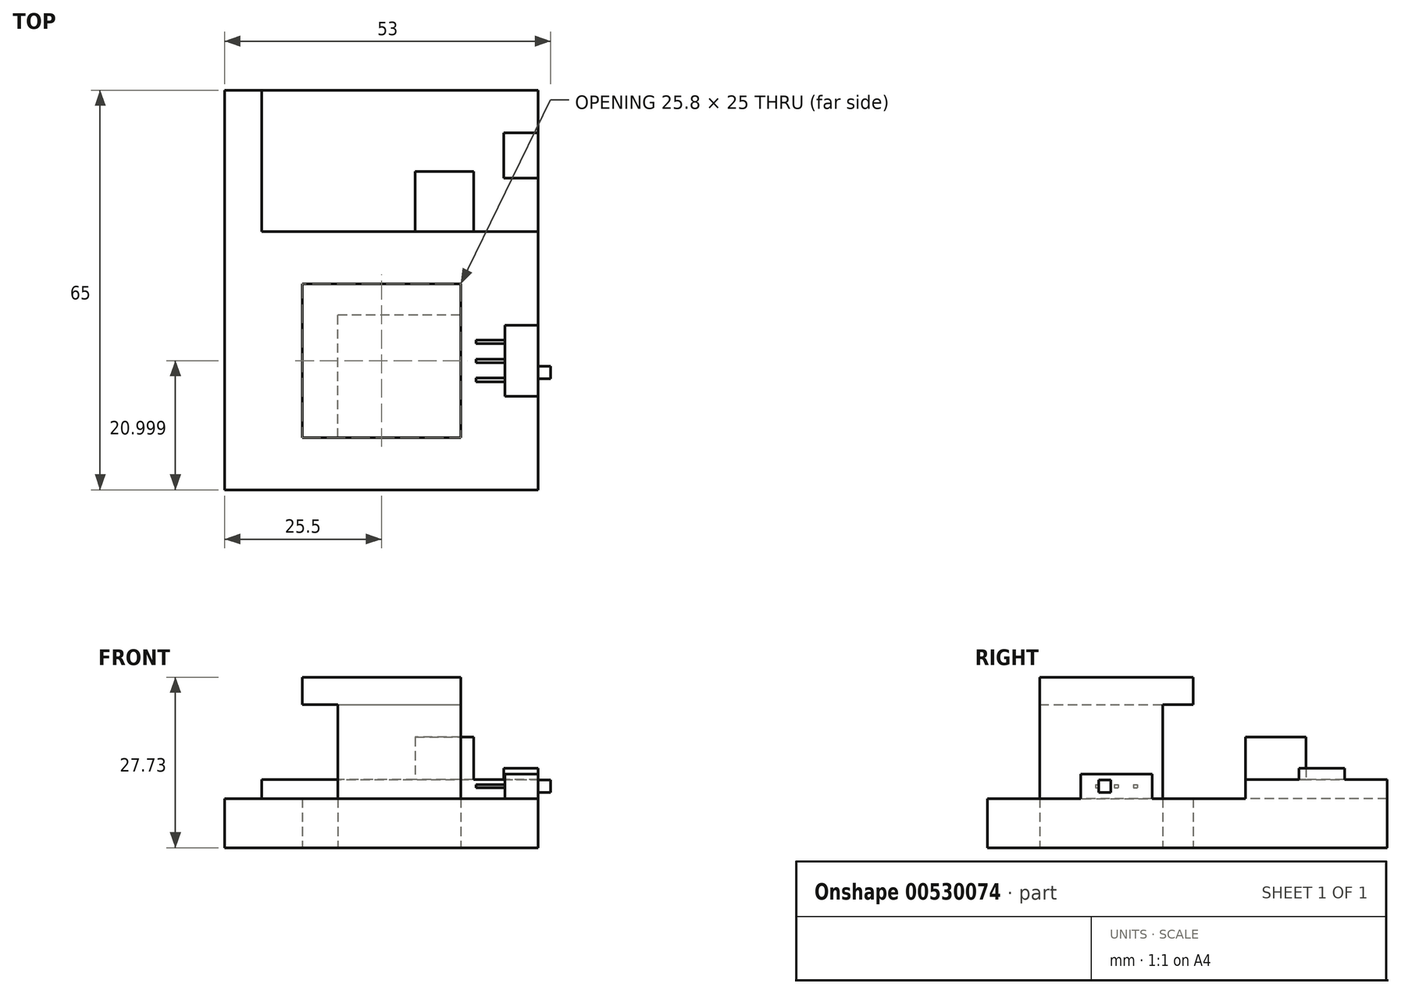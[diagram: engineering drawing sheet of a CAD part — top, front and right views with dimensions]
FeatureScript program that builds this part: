
annotation { "Feature Type Name" : "Feature", "Feature Type Description" : "" }
export const myFeature = defineFeature(function(context is Context, id is Id, definition is map)
    precondition{}
    {
        {
            var Q0;
            Q0=qCreatedBy(makeId("Top.planeOp"),FACE);
            var sketch = newSketch(context, id + "F0", { "sketchPlane" : qUnion([Q0])});
            skLineSegment(sketch, "E0", {"start": v(-31, 10.76) * mm, "end": v(20, 10.76) * mm});
            skLineSegment(sketch, "E1", {"start": v(20, 10.76) * mm, "end": v(20, -54.24) * mm});
            skLineSegment(sketch, "E2", {"start": v(-31, -54.24) * mm, "end": v(-31, 10.76) * mm});
            skLineSegment(sketch, "E3", {"start": v(-31, -54.24) * mm, "end": v(20, -54.24) * mm});
            skLineSegment(sketch, "E4", {"start": v(20, -12.24) * mm, "end": v(-25, -12.24) * mm});
            skLineSegment(sketch, "E5", {"start": v(-25, -12.24) * mm, "end": v(-25, 10.76) * mm});
            skLineSegment(sketch, "E6", {"start": v(20, -3.55) * mm, "end": v(14.37, -3.55) * mm});
            skLineSegment(sketch, "E7", {"start": v(14.37, -3.55) * mm, "end": v(14.37, 3.85) * mm});
            skLineSegment(sketch, "E8", {"start": v(14.37, 3.85) * mm, "end": v(20, 3.85) * mm});
            skLineSegment(sketch, "E9", {"start": v(0, -12.24) * mm, "end": v(0, -2.44) * mm});
            skLineSegment(sketch, "E10", {"start": v(0, -2.44) * mm, "end": v(9.5, -2.44) * mm});
            skLineSegment(sketch, "E11", {"start": v(9.5, -2.44) * mm, "end": v(9.5, -12.24) * mm});
            skLineSegment(sketch, "E12", {"start": v(-18.4, -45.74) * mm, "end": v(7.4, -45.74) * mm});
            skLineSegment(sketch, "E13", {"start": v(-18.4, -20.74) * mm, "end": v(7.4, -20.74) * mm});
            skLineSegment(sketch, "E14", {"start": v(7.4, -45.74) * mm, "end": v(7.4, -20.74) * mm});
            skLineSegment(sketch, "E15", {"start": v(-18.4, -45.74) * mm, "end": v(-18.4, -20.74) * mm});
            skLineSegment(sketch, "E16", {"start": v(-12.6, -45.74) * mm, "end": v(-12.6, -25.74) * mm});
            skLineSegment(sketch, "E17", {"start": v(-12.6, -25.74) * mm, "end": v(7.4, -25.74) * mm});
            skLineSegment(sketch, "E18", {"start": v(14.6, -39.04) * mm, "end": v(20, -39.04) * mm});
            skLineSegment(sketch, "E19", {"start": v(14.6, -27.44) * mm, "end": v(20, -27.44) * mm});
            skLineSegment(sketch, "E20", {"start": v(14.6, -39.04) * mm, "end": v(14.6, -27.44) * mm});
            skPoint(sketch, "E21.orphan", {"position": v(7.4, -39.04) * mm});
            skPoint(sketch, "E22.orphan", {"position": v(7.4, -27.44) * mm});
            skLineSegment(sketch, "E23", {"start": v(9.9, -33.57) * mm, "end": v(14.6, -33.57) * mm});
            skLineSegment(sketch, "E24", {"start": v(9.9, -32.97) * mm, "end": v(14.6, -32.97) * mm});
            skLineSegment(sketch, "E25", {"start": v(9.9, -33.57) * mm, "end": v(9.9, -32.97) * mm});
            skLineSegment(sketch, "E26", {"start": v(14.6, -30.46) * mm, "end": v(9.9, -30.47) * mm});
            skLineSegment(sketch, "E27", {"start": v(9.9, -30.47) * mm, "end": v(9.9, -29.87) * mm});
            skLineSegment(sketch, "E28", {"start": v(9.9, -29.87) * mm, "end": v(14.6, -29.86) * mm});
            skLineSegment(sketch, "E29", {"start": v(14.6, -36.07) * mm, "end": v(9.9, -36.07) * mm});
            skLineSegment(sketch, "E30", {"start": v(9.9, -36.07) * mm, "end": v(9.9, -36.67) * mm});
            skLineSegment(sketch, "E31", {"start": v(9.9, -36.67) * mm, "end": v(14.6, -36.67) * mm});
            skLineSegment(sketch, "E32", {"start": v(20, -36.14) * mm, "end": v(22, -36.14) * mm});
            skLineSegment(sketch, "E33", {"start": v(22, -36.14) * mm, "end": v(22, -34.14) * mm});
            skLineSegment(sketch, "E34", {"start": v(22, -34.14) * mm, "end": v(20, -34.14) * mm});
            skSolve(sketch);
        }
        {
            var Q0;
            {var subQ10=sQuery(id+"F0.wireOp",EDGE,"E2");Q0=makeQuery(id+"F0.imprint","IMPRINT",FACE,{"disambiguationData":[TD([[makeQuery(id+"F0.imprint","IMPRINT",EDGE,{"derivedFrom":subQ10}),-1.0]])]});}
            var Q1;
            {var subQ3=sQuery(id+"F0.wireOp",EDGE,"E16");Q1=makeQuery(id+"F0.imprint","IMPRINT",FACE,{"disambiguationData":[TD([[makeQuery(id+"F0.imprint","IMPRINT",EDGE,{"derivedFrom":subQ3}),-1.0]])]});}
            var Q2;
            {var subQ1=sQuery(id+"F0.wireOp",EDGE,"E13");Q2=makeQuery(id+"F0.imprint","IMPRINT",FACE,{"disambiguationData":[TD([[makeQuery(id+"F0.imprint","IMPRINT",EDGE,{"derivedFrom":subQ1}),-1.0]])]});}
            var Q3;
            {var subQ1=sQuery(id+"F0.wireOp",EDGE,"E5");Q3=makeQuery(id+"F0.imprint","IMPRINT",FACE,{"disambiguationData":[TD([[makeQuery(id+"F0.imprint","IMPRINT",EDGE,{"derivedFrom":subQ1}),-1.0]])]});}
            var Q4;
            {var subQ0=sQuery(id+"F0.wireOp",EDGE,"E9");Q4=makeQuery(id+"F0.imprint","IMPRINT",FACE,{"disambiguationData":[TD([[makeQuery(id+"F0.imprint","IMPRINT",EDGE,{"derivedFrom":subQ0}),-1.0]])]});}
            var Q5;
            {var subQ0=sQuery(id+"F0.wireOp",EDGE,"E6");Q5=makeQuery(id+"F0.imprint","IMPRINT",FACE,{"disambiguationData":[TD([[makeQuery(id+"F0.imprint","IMPRINT",EDGE,{"derivedFrom":subQ0}),-1.0]])]});}
            var Q6;
            {var subQ6=sQuery(id+"F0.wireOp",EDGE,"E18");Q6=makeQuery(id+"F0.imprint","IMPRINT",FACE,{"disambiguationData":[TD([[makeQuery(id+"F0.imprint","IMPRINT",EDGE,{"derivedFrom":subQ6}),1.0]])]});}
            var Q7;
            {var subQ0=sQuery(id+"F0.wireOp",EDGE,"E29");Q7=makeQuery(id+"F0.imprint","IMPRINT",FACE,{"disambiguationData":[TD([[makeQuery(id+"F0.imprint","IMPRINT",EDGE,{"derivedFrom":subQ0}),1.0]])]});}
            var Q8;
            {var subQ0=sQuery(id+"F0.wireOp",EDGE,"E23");Q8=makeQuery(id+"F0.imprint","IMPRINT",FACE,{"disambiguationData":[TD([[makeQuery(id+"F0.imprint","IMPRINT",EDGE,{"derivedFrom":subQ0}),1.0]])]});}
            var Q9;
            {var subQ0=sQuery(id+"F0.wireOp",EDGE,"E26");Q9=makeQuery(id+"F0.imprint","IMPRINT",FACE,{"disambiguationData":[TD([[makeQuery(id+"F0.imprint","IMPRINT",EDGE,{"derivedFrom":subQ0}),-1.0]])]});}
            extrude(context, id + "F1", {"entities" : qUnion([Q0, Q1, Q2, Q3, Q4, Q5, Q6, Q7, Q8, Q9]), "depth" : 8 * mm, "offsetDistance" : 25 * mm});
        }
        {
            var Q0;
            {var subQ2=sQuery(id+"F0.wireOp",EDGE,"E5");Q0=makeQuery(id+"F0.imprint","IMPRINT",FACE,{"disambiguationData":[TD([[makeQuery(id+"F0.imprint","IMPRINT",EDGE,{"derivedFrom":subQ2}),-1.0]])]});}
            var Q1;
            {var subQ0=sQuery(id+"F0.wireOp",EDGE,"E9");Q1=makeQuery(id+"F0.imprint","IMPRINT",FACE,{"disambiguationData":[TD([[makeQuery(id+"F0.imprint","IMPRINT",EDGE,{"derivedFrom":subQ0}),-1.0]])]});}
            var Q2;
            {var subQ0=sQuery(id+"F0.wireOp",EDGE,"E6");Q2=makeQuery(id+"F0.imprint","IMPRINT",FACE,{"disambiguationData":[TD([[makeQuery(id+"F0.imprint","IMPRINT",EDGE,{"derivedFrom":subQ0}),-1.0]])]});}
            extrude(context, id + "F2", {"entities" : qUnion([Q0, Q1, Q2]), "operationType" : NewBodyOperationType.ADD, "depth" : 11.1 * mm, "offsetDistance" : 25 * mm});
        }
        {
            var Q0;
            {var subQ0=sQuery(id+"F0.wireOp",EDGE,"E6");Q0=makeQuery(id+"F0.imprint","IMPRINT",FACE,{"disambiguationData":[TD([[makeQuery(id+"F0.imprint","IMPRINT",EDGE,{"derivedFrom":subQ0}),-1.0]])]});}
            extrude(context, id + "F3", {"entities" : qUnion([Q0]), "operationType" : NewBodyOperationType.ADD, "depth" : 12.95 * mm, "offsetDistance" : 25 * mm});
        }
        {
            var Q0;
            {var subQ0=sQuery(id+"F0.wireOp",EDGE,"E9");Q0=makeQuery(id+"F0.imprint","IMPRINT",FACE,{"disambiguationData":[TD([[makeQuery(id+"F0.imprint","IMPRINT",EDGE,{"derivedFrom":subQ0}),-1.0]])]});}
            extrude(context, id + "F4", {"entities" : qUnion([Q0]), "operationType" : NewBodyOperationType.ADD, "depth" : 18 * mm, "offsetDistance" : 25 * mm});
        }
        {
            var Q0;
            {var subQ3=sQuery(id+"F0.wireOp",EDGE,"E16");Q0=makeQuery(id+"F0.imprint","IMPRINT",FACE,{"disambiguationData":[TD([[makeQuery(id+"F0.imprint","IMPRINT",EDGE,{"derivedFrom":subQ3}),-1.0]])]});}
            extrude(context, id + "F5", {"entities" : qUnion([Q0]), "operationType" : NewBodyOperationType.ADD, "depth" : 23.3 * mm, "offsetDistance" : 25 * mm});
        }
        {
            var Q0;
            {var subQ3=sQuery(id+"F0.wireOp",EDGE,"E16");Q0=makeQuery(id+"F0.imprint","IMPRINT",FACE,{"disambiguationData":[TD([[makeQuery(id+"F0.imprint","IMPRINT",EDGE,{"derivedFrom":subQ3}),-1.0]])]});}
            var Q1;
            {var subQ1=sQuery(id+"F0.wireOp",EDGE,"E13");Q1=makeQuery(id+"F0.imprint","IMPRINT",FACE,{"disambiguationData":[TD([[makeQuery(id+"F0.imprint","IMPRINT",EDGE,{"derivedFrom":subQ1}),-1.0]])]});}
            extrude(context, id + "F6", {"entities" : qUnion([Q0, Q1]), "operationType" : NewBodyOperationType.ADD, "depth" : 27.73 * mm, "offsetDistance" : 25 * mm});
        }
        {
            var Q0;
            {var subQ1=sQuery(id+"F0.wireOp",EDGE,"E13");Q0=makeQuery(id+"F0.imprint","IMPRINT",FACE,{"disambiguationData":[TD([[makeQuery(id+"F0.imprint","IMPRINT",EDGE,{"derivedFrom":subQ1}),-1.0]])]});}
            extrude(context, id + "F7", {"entities" : qUnion([Q0]), "operationType" : NewBodyOperationType.REMOVE, "depth" : 23.3 * mm, "offsetDistance" : 25 * mm});
        }
        {
            var Q0;
            {var subQ1=sQuery(id+"F0.wireOp",EDGE,"E13");Q0=makeQuery(id+"F0.imprint","IMPRINT",FACE,{"disambiguationData":[TD([[makeQuery(id+"F0.imprint","IMPRINT",EDGE,{"derivedFrom":subQ1}),-1.0]])]});}
            extrude(context, id + "F8", {"entities" : qUnion([Q0]), "depth" : 8 * mm, "offsetDistance" : 25 * mm});
        }
        {
            var Q0;
            {var subQ6=sQuery(id+"F0.wireOp",EDGE,"E18");Q0=makeQuery(id+"F0.imprint","IMPRINT",FACE,{"disambiguationData":[TD([[makeQuery(id+"F0.imprint","IMPRINT",EDGE,{"derivedFrom":subQ6}),1.0]])]});}
            extrude(context, id + "F9", {"entities" : qUnion([Q0]), "operationType" : NewBodyOperationType.ADD, "depth" : 12 * mm, "offsetDistance" : 25 * mm});
        }
        {
            var Q0;
            {var subQ0=sQuery(id+"F0.wireOp",EDGE,"E26");Q0=makeQuery(id+"F0.imprint","IMPRINT",FACE,{"disambiguationData":[TD([[makeQuery(id+"F0.imprint","IMPRINT",EDGE,{"derivedFrom":subQ0}),-1.0]])]});}
            var Q1;
            {var subQ0=sQuery(id+"F0.wireOp",EDGE,"E23");Q1=makeQuery(id+"F0.imprint","IMPRINT",FACE,{"disambiguationData":[TD([[makeQuery(id+"F0.imprint","IMPRINT",EDGE,{"derivedFrom":subQ0}),1.0]])]});}
            var Q2;
            {var subQ0=sQuery(id+"F0.wireOp",EDGE,"E29");Q2=makeQuery(id+"F0.imprint","IMPRINT",FACE,{"disambiguationData":[TD([[makeQuery(id+"F0.imprint","IMPRINT",EDGE,{"derivedFrom":subQ0}),1.0]])]});}
            extrude(context, id + "F10", {"entities" : qUnion([Q0, Q1, Q2]), "operationType" : NewBodyOperationType.ADD, "depth" : 10.25 * mm, "offsetDistance" : 25 * mm});
        }
        {
            var Q0;
            {var subQ0=sQuery(id+"F0.wireOp",EDGE,"E26");Q0=makeQuery(id+"F0.imprint","IMPRINT",FACE,{"disambiguationData":[TD([[makeQuery(id+"F0.imprint","IMPRINT",EDGE,{"derivedFrom":subQ0}),-1.0]])]});}
            var Q1;
            {var subQ0=sQuery(id+"F0.wireOp",EDGE,"E23");Q1=makeQuery(id+"F0.imprint","IMPRINT",FACE,{"disambiguationData":[TD([[makeQuery(id+"F0.imprint","IMPRINT",EDGE,{"derivedFrom":subQ0}),1.0]])]});}
            var Q2;
            {var subQ0=sQuery(id+"F0.wireOp",EDGE,"E29");Q2=makeQuery(id+"F0.imprint","IMPRINT",FACE,{"disambiguationData":[TD([[makeQuery(id+"F0.imprint","IMPRINT",EDGE,{"derivedFrom":subQ0}),1.0]])]});}
            extrude(context, id + "F11", {"entities" : qUnion([Q0, Q1, Q2]), "operationType" : NewBodyOperationType.REMOVE, "depth" : 9.75 * mm, "offsetDistance" : 25 * mm});
        }
        {
            var Q0;
            {var subQ0=sQuery(id+"F0.wireOp",EDGE,"E29");Q0=makeQuery(id+"F0.imprint","IMPRINT",FACE,{"disambiguationData":[TD([[makeQuery(id+"F0.imprint","IMPRINT",EDGE,{"derivedFrom":subQ0}),1.0]])]});}
            var Q1;
            {var subQ0=sQuery(id+"F0.wireOp",EDGE,"E23");Q1=makeQuery(id+"F0.imprint","IMPRINT",FACE,{"disambiguationData":[TD([[makeQuery(id+"F0.imprint","IMPRINT",EDGE,{"derivedFrom":subQ0}),1.0]])]});}
            var Q2;
            {var subQ0=sQuery(id+"F0.wireOp",EDGE,"E26");Q2=makeQuery(id+"F0.imprint","IMPRINT",FACE,{"disambiguationData":[TD([[makeQuery(id+"F0.imprint","IMPRINT",EDGE,{"derivedFrom":subQ0}),-1.0]])]});}
            extrude(context, id + "F12", {"entities" : qUnion([Q0, Q1, Q2]), "operationType" : NewBodyOperationType.ADD, "depth" : 8 * mm, "offsetDistance" : 25 * mm});
        }
        {
            var Q0;
            {var subQ0=sQuery(id+"F0.wireOp",EDGE,"E32");Q0=makeQuery(id+"F0.imprint","IMPRINT",FACE,{"disambiguationData":[TD([[makeQuery(id+"F0.imprint","IMPRINT",EDGE,{"derivedFrom":subQ0}),1.0]])]});}
            extrude(context, id + "F13", {"entities" : qUnion([Q0]), "operationType" : NewBodyOperationType.ADD, "depth" : 11 * mm, "offsetDistance" : 25 * mm});
        }
        {
            var Q0;
            {var subQ0=sQuery(id+"F0.wireOp",EDGE,"E32");Q0=makeQuery(id+"F0.imprint","IMPRINT",FACE,{"disambiguationData":[TD([[makeQuery(id+"F0.imprint","IMPRINT",EDGE,{"derivedFrom":subQ0}),1.0]])]});}
            extrude(context, id + "F14", {"entities" : qUnion([Q0]), "operationType" : NewBodyOperationType.REMOVE, "depth" : 9 * mm, "offsetDistance" : 25 * mm});
        }
    });
